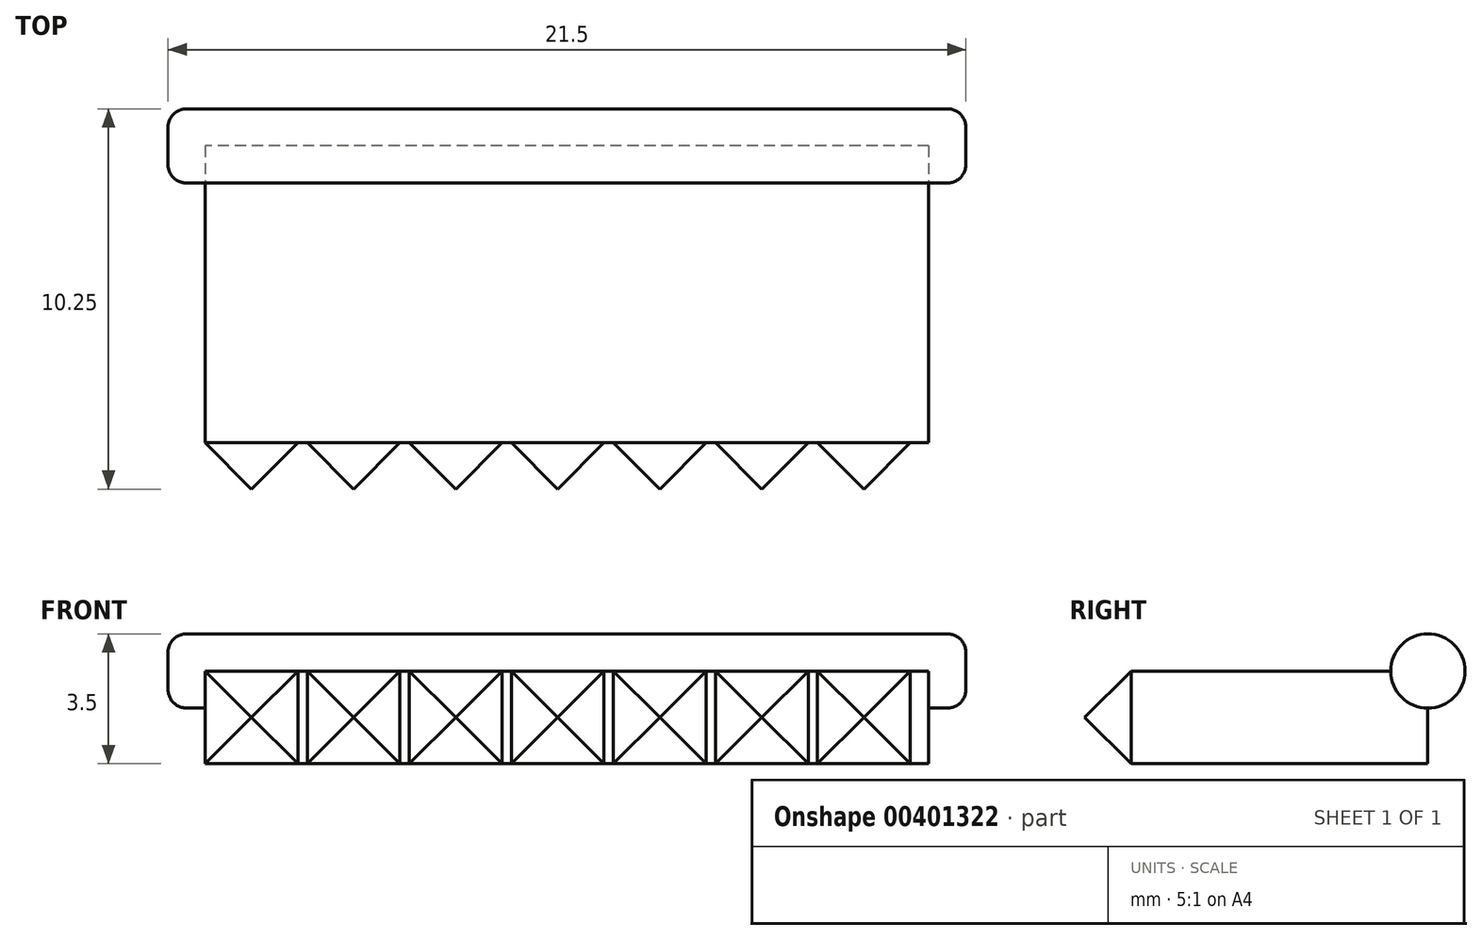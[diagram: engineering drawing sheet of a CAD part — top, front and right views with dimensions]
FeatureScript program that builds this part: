
annotation { "Feature Type Name" : "Feature", "Feature Type Description" : "" }
export const myFeature = defineFeature(function(context is Context, id is Id, definition is map)
    precondition{}
    {
        {
            var Q0;
            Q0=qCreatedBy(makeId("Top.planeOp"),FACE);
            var sketch = newSketch(context, id + "F0", { "sketchPlane" : qUnion([Q0])});
            skLineSegment(sketch, "E0.bottom", {"start": v(0, 0) * mm, "end": v(-19.5, 0) * mm});
            skLineSegment(sketch, "E0.top", {"start": v(0, -8) * mm, "end": v(-19.5, -8) * mm});
            skLineSegment(sketch, "E0.left", {"start": v(0, 0) * mm, "end": v(0, -8) * mm});
            skLineSegment(sketch, "E0.right", {"start": v(-19.5, 0) * mm, "end": v(-19.5, -8) * mm});
            skSolve(sketch);
        }
        {
            var Q0;
            Q0 = qSketchRegion(id + "F0", true);
            extrude(context, id + "F1", {"entities" : qUnion([Q0]), "oppositeDirection" : true, "depth" : 2.5 * mm});
        }
        {
            var Q0;
            Q0=qCreatedBy(makeId("Right.planeOp"),FACE);
            var sketch = newSketch(context, id + "F2", { "sketchPlane" : qUnion([Q0])});
            skCircle(sketch, "E1", {"center": v(0, 0) * mm, "radius": 1 * mm});
            skSolve(sketch);
        }
        {
            var Q0;
            Q0 = qSketchRegion(id + "F2", true);
            extrude(context, id + "F3", {"entities" : qUnion([Q0]), "operationType" : NewBodyOperationType.ADD, "depth" : 1 * mm, "hasSecondDirection" : true, "secondDirectionOppositeDirection" : true, "secondDirectionDepth" : 20.5 * mm});
        }
        {
            var Q0;
            Q0=makeQuery(id+"F3.opExtrude","CAP_EDGE",EDGE,{"disambiguationData":[OSD([sQuery(id+"F2.wireOp",EDGE,"E1")])],"isStart":true});
            var Q1;
            Q1=makeQuery(id+"F3.opExtrude","CAP_EDGE",EDGE,{"disambiguationData":[OSD([sQuery(id+"F2.wireOp",EDGE,"E1")])],"isStart":false});
            fillet(context, id + "F4", {"entities" : qUnion([Q0, Q1]), "radius" : .5 * mm, "tangentPropagation" : true, "allowEdgeOverflow" : false});
        }
        {
            var Q0;
            Q0=makeQuery(id+"F1.opExtrude","SWEPT_FACE",FACE,{"disambiguationData":[OSD([sQuery(id+"F0.wireOp",EDGE,"E0.top")])]});
            var sketch = newSketch(context, id + "F5", { "sketchPlane" : qUnion([Q0])});
            skLineSegment(sketch, "E2.bottom", {"start": v(-19.5, -2.5) * mm, "end": v(-17, -2.5) * mm});
            skLineSegment(sketch, "E2.top", {"start": v(-19.5, 0) * mm, "end": v(-17, 0) * mm});
            skLineSegment(sketch, "E2.left", {"start": v(-19.5, -2.5) * mm, "end": v(-19.5, 0) * mm});
            skLineSegment(sketch, "E2.right", {"start": v(-17, -2.5) * mm, "end": v(-17, 0) * mm});
            skLineSegment(sketch, "E3.1.0.0", {"start": v(-14.25, -2.5) * mm, "end": v(-14.25, 0) * mm});
            skLineSegment(sketch, "E3.1.0.1", {"start": v(-16.75, 0) * mm, "end": v(-14.25, 0) * mm});
            skLineSegment(sketch, "E3.1.0.2", {"start": v(-16.75, -2.5) * mm, "end": v(-16.75, 0) * mm});
            skLineSegment(sketch, "E3.1.0.3", {"start": v(-16.75, -2.5) * mm, "end": v(-14.25, -2.5) * mm});
            skLineSegment(sketch, "E3.2.0.0", {"start": v(-11.5, -2.5) * mm, "end": v(-11.5, 0) * mm});
            skLineSegment(sketch, "E3.2.0.1", {"start": v(-14, 0) * mm, "end": v(-11.5, 0) * mm});
            skLineSegment(sketch, "E3.2.0.2", {"start": v(-14, -2.5) * mm, "end": v(-14, 0) * mm});
            skLineSegment(sketch, "E3.2.0.3", {"start": v(-14, -2.5) * mm, "end": v(-11.5, -2.5) * mm});
            skLineSegment(sketch, "E3.direction1", {"start": v(-17, -2.5) * mm, "end": v(-14.25, -2.5) * mm, "construction": true});
            skLineSegment(sketch, "E4.0.3.0", {"start": v(-8.75, -2.5) * mm, "end": v(-8.75, 0) * mm});
            skLineSegment(sketch, "E4.3.3.0", {"start": v(-11.25, 0) * mm, "end": v(-8.75, 0) * mm});
            skLineSegment(sketch, "E4.6.3.0", {"start": v(-11.25, -2.5) * mm, "end": v(-11.25, 0) * mm});
            skLineSegment(sketch, "E4.9.3.0", {"start": v(-11.25, -2.5) * mm, "end": v(-8.75, -2.5) * mm});
            skLineSegment(sketch, "E4.0.4.0", {"start": v(-6, -2.5) * mm, "end": v(-6, 0) * mm});
            skLineSegment(sketch, "E4.3.4.0", {"start": v(-8.5, 0) * mm, "end": v(-6, 0) * mm});
            skLineSegment(sketch, "E4.6.4.0", {"start": v(-8.5, -2.5) * mm, "end": v(-8.5, 0) * mm});
            skLineSegment(sketch, "E4.9.4.0", {"start": v(-8.5, -2.5) * mm, "end": v(-6, -2.5) * mm});
            skLineSegment(sketch, "E4.0.5.0", {"start": v(-3.25, -2.5) * mm, "end": v(-3.25, 0) * mm});
            skLineSegment(sketch, "E4.3.5.0", {"start": v(-5.75, 0) * mm, "end": v(-3.25, 0) * mm});
            skLineSegment(sketch, "E4.6.5.0", {"start": v(-5.75, -2.5) * mm, "end": v(-5.75, 0) * mm});
            skLineSegment(sketch, "E4.9.5.0", {"start": v(-5.75, -2.5) * mm, "end": v(-3.25, -2.5) * mm});
            skLineSegment(sketch, "E5.0.6.0", {"start": v(-0.5, -2.5) * mm, "end": v(-0.5, 0) * mm});
            skLineSegment(sketch, "E5.3.6.0", {"start": v(-3, 0) * mm, "end": v(-0.5, 0) * mm});
            skLineSegment(sketch, "E5.6.6.0", {"start": v(-3, -2.5) * mm, "end": v(-3, 0) * mm});
            skLineSegment(sketch, "E5.9.6.0", {"start": v(-3, -2.5) * mm, "end": v(-0.5, -2.5) * mm});
            skSolve(sketch);
        }
        {
            var Q0;
            Q0 = qSketchRegion(id + "F5", true);
            extrude(context, id + "F6", {"entities" : qUnion([Q0]), "operationType" : NewBodyOperationType.ADD, "depth" : 25 * mm, "hasDraft" : true, "draftAngle" : 45 * degree, "draftPullDirection" : true});
        }
    });
